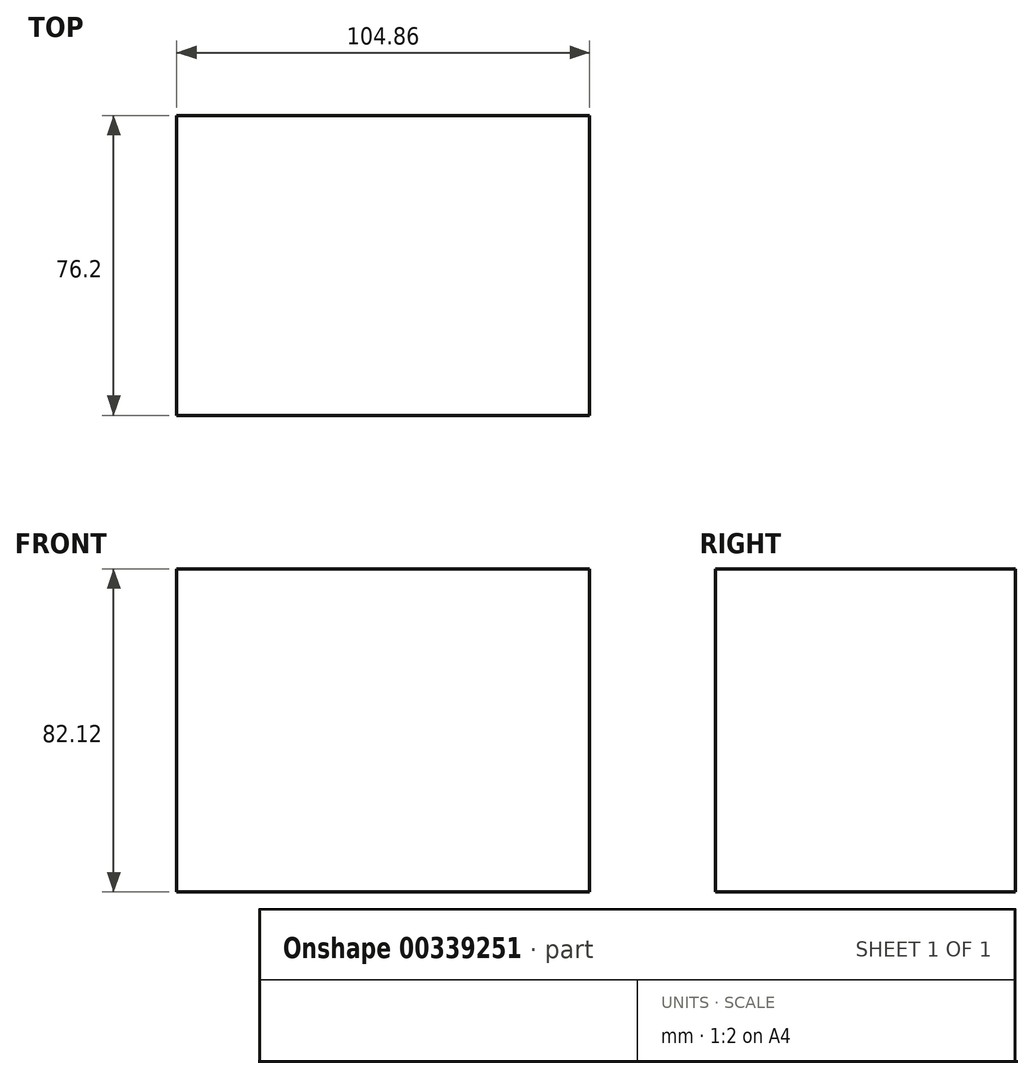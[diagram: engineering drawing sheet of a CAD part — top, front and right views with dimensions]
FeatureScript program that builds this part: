
annotation { "Feature Type Name" : "Feature", "Feature Type Description" : "" }
export const myFeature = defineFeature(function(context is Context, id is Id, definition is map)
    precondition{}
    {
        {
            var Q0;
            Q0=qCreatedBy(makeId("Front.planeOp"),FACE);
            var sketch = newSketch(context, id + "F0", { "sketchPlane" : qUnion([Q0])});
            skLineSegment(sketch, "E0.bottom", {"start": v(52.43, 41.06) * mm, "end": v(-52.43, 41.06) * mm});
            skLineSegment(sketch, "E0.top", {"start": v(52.43, -41.06) * mm, "end": v(-52.43, -41.06) * mm});
            skLineSegment(sketch, "E0.left", {"start": v(52.43, 41.06) * mm, "end": v(52.43, -41.06) * mm});
            skLineSegment(sketch, "E0.right", {"start": v(-52.43, 41.06) * mm, "end": v(-52.43, -41.06) * mm});
            skPoint(sketch, "E0.middle", {"position": v(0, 0) * mm});
            skSolve(sketch);
        }
        {
            var Q0;
            Q0=makeQuery(id+"F0.imprint","IMPRINT",FACE,{"disambiguationData":[TD([[makeQuery(id+"F0.imprint","IMPRINT",EDGE,{"derivedFrom":sQuery(id+"F0.wireOp",EDGE,"E0.bottom")}),1.0]])]});
            extrude(context, id + "F1", {"entities" : qUnion([Q0]), "depth" : 76.2 * mm});
        }
    });
